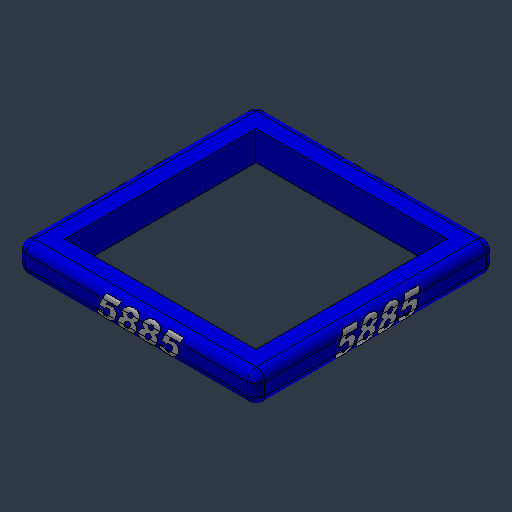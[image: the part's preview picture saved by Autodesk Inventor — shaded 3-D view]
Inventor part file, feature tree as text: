
AUTODESK INVENTOR PART (.ipt)
format: ipt  version: 2024.3 (Build 283343000, 343)  size: 1,186,816 bytes
history: native  units: mm (DEFAULTED — no unit token found)
features: other x3, move_body x2, direct_edit x1, emboss x1, pattern_circular x1, sketch x1
ambient origin geometry x8: Origin, YZ Plane, XZ Plane, XY Plane, X Axis, Y Axis, Z Axis, Center Point
bodies: Solid1 (feature_tree)
feature tree (9):
  other  "2025 Bumper Fabric.ipt"
  direct_edit  "Direct Edit1"
  emboss  "Emboss1"
  pattern_circular  "Circular Pattern1"  [2 undecoded]
  other  "Solid1::2025 Bumper Fabric.ipt"
  other  "TaggingFeature1"
  sketch  "Sketch2"  dims[d0=10.0mm d1=0.254mm d2=0.0mm d3=0.0mm d4=0.0mm d5=269.846692mm d6=0.0mm d7=-381.0mm d8=0.0mm d9=40.0mm d10=360.0deg]
  move_body  "Move1"
  move_body  "Move2"
note: 2 required parameter values undecoded (feature->parameter linkage not recoverable at this tier; creation-order binding heuristic only, values carry confidence <= 0.55)
